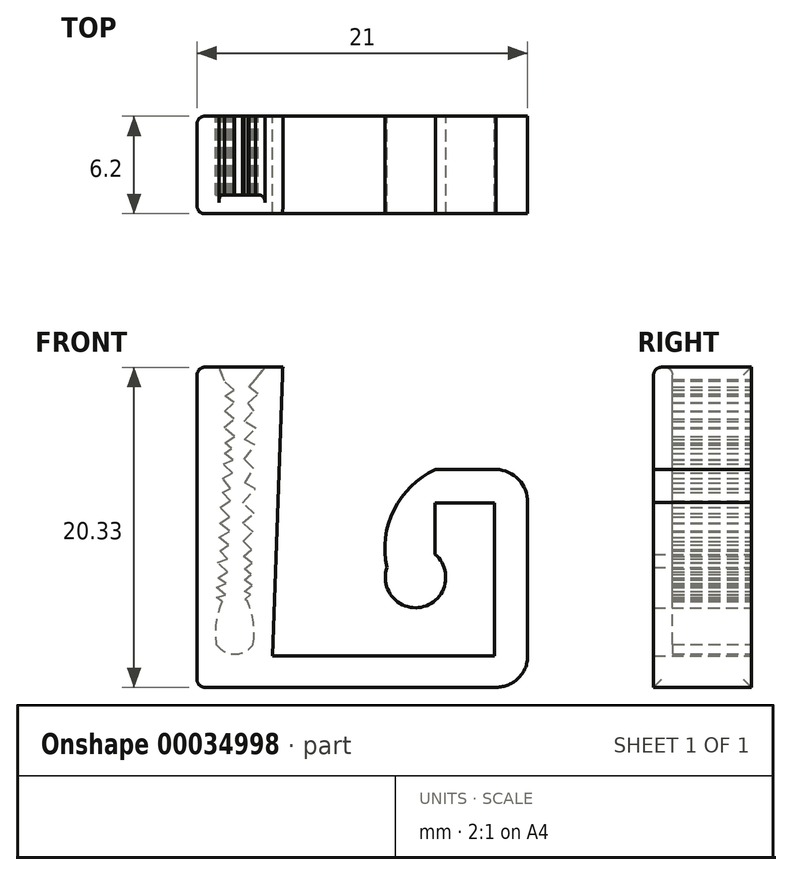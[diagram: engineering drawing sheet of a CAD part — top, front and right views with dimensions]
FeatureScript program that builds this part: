
annotation { "Feature Type Name" : "Feature", "Feature Type Description" : "" }
export const myFeature = defineFeature(function(context is Context, id is Id, definition is map)
    precondition{}
    {
        {
            var Q0;
            Q0=qCreatedBy(makeId("Front.planeOp"),FACE);
            var sketch = newSketch(context, id + "F0", { "sketchPlane" : qUnion([Q0])});
            skLineSegment(sketch, "E0", {"start": v(-28.92, -7.05) * mm, "end": v(-14.82, -7.05) * mm});
            skLineSegment(sketch, "E1", {"start": v(-14.82, -7.05) * mm, "end": v(-14.82, 2.65) * mm});
            skArc(sketch, "E2", {"start": v(-18.58, 4.78) * mm, "mid": v(-21.22, 2.2) * mm, "end": v(-21.65, -1.46) * mm});
            skArc(sketch, "E3", {"start": v(-21.65, -1.46) * mm, "mid": v(-19.32, -3.93) * mm, "end": v(-18.62, -0.6) * mm});
            skLineSegment(sketch, "E4", {"start": v(-18.62, 2.65) * mm, "end": v(-18.62, -0.6) * mm});
            skLineSegment(sketch, "E5.top", {"start": v(-28.92, 11.27) * mm, "end": v(-29.4, 11.27) * mm});
            skLineSegment(sketch, "E6", {"start": v(-18.62, 2.65) * mm, "end": v(-14.82, 2.65) * mm});
            skLineSegment(sketch, "E7", {"start": v(-33.72, 11.27) * mm, "end": v(-33.72, -9.05) * mm});
            skLineSegment(sketch, "E8", {"start": v(-30.52, -7.05) * mm, "end": v(-32.12, -7.05) * mm, "construction": true});
            skLineSegment(sketch, "E9", {"start": v(-21.65, -1.46) * mm, "end": v(-18.62, -0.6) * mm, "construction": true});
            skLineSegment(sketch, "E10", {"start": v(-31.32, -5.22) * mm, "end": v(-31.32, -1.98) * mm, "construction": true});
            skLineSegment(sketch, "E11.MirrorCS", {"start": v(-30.52, 11.27) * mm, "end": v(-32.12, 11.27) * mm, "construction": true});
            skArc(sketch, "E12", {"start": v(-32.12, -3.61) * mm, "mid": v(-32.5, -4.94) * mm, "end": v(-32.5, -6.32) * mm});
            skArc(sketch, "E13", {"start": v(-32.5, -6.32) * mm, "mid": v(-31.32, -6.95) * mm, "end": v(-30.15, -6.32) * mm});
            skArc(sketch, "E14.MirrorCS", {"start": v(-30.52, -3.61) * mm, "mid": v(-30.14, -4.94) * mm, "end": v(-30.15, -6.32) * mm});
            skArc(sketch, "E15", {"start": v(-12.72, 2.65) * mm, "mid": v(-13.28, 4.13) * mm, "end": v(-14.72, 4.78) * mm});
            skLineSegment(sketch, "E16", {"start": v(-14.72, 4.78) * mm, "end": v(-18.58, 4.78) * mm});
            skArc(sketch, "E17", {"start": v(-14.82, -9.05) * mm, "mid": v(-13.34, -8.5) * mm, "end": v(-12.72, -7.05) * mm});
            skLineSegment(sketch, "E18", {"start": v(-14.82, -9.05) * mm, "end": v(-33.72, -9.05) * mm});
            skLineSegment(sketch, "E19", {"start": v(-12.72, -7.05) * mm, "end": v(-12.72, 2.68) * mm});
            skLineSegment(sketch, "E20", {"start": v(-28.92, -7.05) * mm, "end": v(-28.27, 11.27) * mm});
            skLineSegment(sketch, "E21", {"start": v(-28.27, 11.27) * mm, "end": v(-28.92, 11.27) * mm});
            skLineSegment(sketch, "E22", {"start": v(-32.12, -3.61) * mm, "end": v(-32.5, -3.36) * mm});
            skLineSegment(sketch, "E23", {"start": v(-32.5, -3.36) * mm, "end": v(-31.9, -3.2) * mm});
            skLineSegment(sketch, "E24", {"start": v(-31.9, -3.2) * mm, "end": v(-32.47, -2.73) * mm});
            skLineSegment(sketch, "E25", {"start": v(-32.47, -2.73) * mm, "end": v(-31.87, -2.47) * mm});
            skLineSegment(sketch, "E26", {"start": v(-31.87, -2.47) * mm, "end": v(-32.37, -2.11) * mm});
            skLineSegment(sketch, "E27", {"start": v(-32.37, -2.11) * mm, "end": v(-31.8, -1.73) * mm});
            skLineSegment(sketch, "E28", {"start": v(-31.8, -1.73) * mm, "end": v(-32.4, -1.14) * mm});
            skLineSegment(sketch, "E29", {"start": v(-32.4, -1.14) * mm, "end": v(-31.79, -0.91) * mm});
            skLineSegment(sketch, "E30", {"start": v(-31.79, -0.91) * mm, "end": v(-32.26, -0.4) * mm});
            skLineSegment(sketch, "E31", {"start": v(-32.26, -0.4) * mm, "end": v(-31.73, 0) * mm});
            skLineSegment(sketch, "E32", {"start": v(-31.73, 0) * mm, "end": v(-32.3, 0.46) * mm});
            skLineSegment(sketch, "E33", {"start": v(-32.3, 0.46) * mm, "end": v(-31.65, 0.87) * mm});
            skLineSegment(sketch, "E34", {"start": v(-31.65, 0.87) * mm, "end": v(-32.28, 1.36) * mm});
            skLineSegment(sketch, "E35", {"start": v(-32.28, 1.36) * mm, "end": v(-31.67, 1.76) * mm});
            skLineSegment(sketch, "E36", {"start": v(-31.67, 1.76) * mm, "end": v(-32.25, 2.38) * mm});
            skLineSegment(sketch, "E37", {"start": v(-32.25, 2.38) * mm, "end": v(-31.6, 2.77) * mm});
            skLineSegment(sketch, "E38", {"start": v(-31.6, 2.77) * mm, "end": v(-32.08, 3.3) * mm});
            skLineSegment(sketch, "E39", {"start": v(-32.08, 3.3) * mm, "end": v(-31.58, 3.56) * mm});
            skLineSegment(sketch, "E40", {"start": v(-31.58, 3.56) * mm, "end": v(-32.1, 4.22) * mm});
            skLineSegment(sketch, "E41", {"start": v(-32.1, 4.22) * mm, "end": v(-31.45, 4.55) * mm});
            skLineSegment(sketch, "E42", {"start": v(-31.45, 4.55) * mm, "end": v(-32.05, 5.14) * mm});
            skLineSegment(sketch, "E43", {"start": v(-32.05, 5.14) * mm, "end": v(-31.42, 5.37) * mm});
            skLineSegment(sketch, "E44", {"start": v(-31.42, 5.37) * mm, "end": v(-31.96, 5.8) * mm});
            skLineSegment(sketch, "E45", {"start": v(-31.96, 5.8) * mm, "end": v(-31.54, 6.12) * mm});
            skLineSegment(sketch, "E46", {"start": v(-31.54, 6.12) * mm, "end": v(-31.94, 6.47) * mm});
            skLineSegment(sketch, "E47", {"start": v(-31.94, 6.47) * mm, "end": v(-31.32, 6.88) * mm});
            skLineSegment(sketch, "E48", {"start": v(-31.32, 6.88) * mm, "end": v(-32.01, 7.44) * mm});
            skLineSegment(sketch, "E49", {"start": v(-32.01, 7.44) * mm, "end": v(-31.35, 7.98) * mm});
            skLineSegment(sketch, "E50", {"start": v(-31.35, 7.98) * mm, "end": v(-31.96, 8.46) * mm});
            skLineSegment(sketch, "E51", {"start": v(-31.96, 8.46) * mm, "end": v(-31.38, 9.02) * mm});
            skLineSegment(sketch, "E52", {"start": v(-31.38, 9.02) * mm, "end": v(-31.93, 9.43) * mm});
            skLineSegment(sketch, "E53", {"start": v(-31.93, 9.43) * mm, "end": v(-31.38, 9.83) * mm});
            skLineSegment(sketch, "E54", {"start": v(-31.38, 9.83) * mm, "end": v(-31.97, 10.39) * mm});
            skLineSegment(sketch, "E55", {"start": v(-30.52, -3.61) * mm, "end": v(-30.66, -3.49) * mm});
            skLineSegment(sketch, "E56", {"start": v(-30.66, -3.49) * mm, "end": v(-30.3, -3.14) * mm});
            skLineSegment(sketch, "E57", {"start": v(-30.3, -3.14) * mm, "end": v(-30.69, -2.97) * mm});
            skLineSegment(sketch, "E58", {"start": v(-30.69, -2.97) * mm, "end": v(-30.24, -2.58) * mm});
            skLineSegment(sketch, "E59", {"start": v(-30.24, -2.58) * mm, "end": v(-30.7, -2.24) * mm});
            skLineSegment(sketch, "E60", {"start": v(-30.7, -2.24) * mm, "end": v(-30.27, -1.87) * mm});
            skLineSegment(sketch, "E61", {"start": v(-30.27, -1.87) * mm, "end": v(-30.7, -1.53) * mm});
            skLineSegment(sketch, "E62", {"start": v(-30.7, -1.53) * mm, "end": v(-30.22, -1.16) * mm});
            skLineSegment(sketch, "E63", {"start": v(-30.22, -1.16) * mm, "end": v(-30.76, -0.74) * mm});
            skLineSegment(sketch, "E64", {"start": v(-30.76, -0.74) * mm, "end": v(-30.24, -0.31) * mm});
            skLineSegment(sketch, "E65", {"start": v(-30.24, -0.31) * mm, "end": v(-30.79, 0.22) * mm});
            skLineSegment(sketch, "E66", {"start": v(-30.79, 0.22) * mm, "end": v(-30.15, 0.82) * mm});
            skLineSegment(sketch, "E67", {"start": v(-30.15, 0.82) * mm, "end": v(-30.83, 1.4) * mm});
            skLineSegment(sketch, "E68", {"start": v(-30.83, 1.4) * mm, "end": v(-30.1, 2) * mm});
            skLineSegment(sketch, "E69", {"start": v(-30.1, 2) * mm, "end": v(-30.84, 2.67) * mm});
            skLineSegment(sketch, "E70", {"start": v(-30.84, 2.67) * mm, "end": v(-30.01, 3.55) * mm});
            skLineSegment(sketch, "E71", {"start": v(-30.01, 3.55) * mm, "end": v(-30.68, 3.92) * mm});
            skLineSegment(sketch, "E72", {"start": v(-30.68, 3.92) * mm, "end": v(-30.13, 4.84) * mm});
            skLineSegment(sketch, "E73", {"start": v(-30.13, 4.84) * mm, "end": v(-30.72, 5.42) * mm});
            skLineSegment(sketch, "E74", {"start": v(-30.72, 5.42) * mm, "end": v(-30.04, 6.32) * mm});
            skLineSegment(sketch, "E75", {"start": v(-30.04, 6.32) * mm, "end": v(-30.7, 6.7) * mm});
            skLineSegment(sketch, "E76", {"start": v(-30.7, 6.7) * mm, "end": v(-29.98, 7.38) * mm});
            skLineSegment(sketch, "E77", {"start": v(-29.98, 7.38) * mm, "end": v(-30.73, 7.84) * mm});
            skLineSegment(sketch, "E78", {"start": v(-30.73, 7.84) * mm, "end": v(-30.11, 8.5) * mm});
            skLineSegment(sketch, "E79", {"start": v(-30.11, 8.5) * mm, "end": v(-30.46, 9) * mm});
            skLineSegment(sketch, "E80", {"start": v(-30.46, 9) * mm, "end": v(-29.84, 9.59) * mm});
            skLineSegment(sketch, "E81", {"start": v(-29.84, 9.59) * mm, "end": v(-30.41, 10.01) * mm});
            skLineSegment(sketch, "E82", {"start": v(-30.41, 10.01) * mm, "end": v(-30, 10.48) * mm});
            skLineSegment(sketch, "E83", {"start": v(-30, 10.48) * mm, "end": v(-29.4, 11.27) * mm});
            skLineSegment(sketch, "E84", {"start": v(-31.97, 10.39) * mm, "end": v(-32.33, 11.27) * mm});
            skLineSegment(sketch, "E85", {"start": v(-32.33, 11.27) * mm, "end": v(-33.72, 11.27) * mm});
            skSolve(sketch);
        }
        {
            var Q0;
            Q0 = qSketchRegion(id + "F0", true);
            extrude(context, id + "F1", {"entities" : qUnion([Q0]), "depth" : 5 * mm});
        }
        {
            var Q0;
            Q0=makeQuery(id+"F1.opExtrude","CAP_FACE",FACE,{"disambiguationData":[OSD([sQuery(id+"F0.wireOp",EDGE,"E0"),sQuery(id+"F0.wireOp",EDGE,"E1"),sQuery(id+"F0.wireOp",EDGE,"E2"),sQuery(id+"F0.wireOp",EDGE,"E3"),sQuery(id+"F0.wireOp",EDGE,"E4"),sQuery(id+"F0.wireOp",EDGE,"E5.top"),sQuery(id+"F0.wireOp",EDGE,"E6"),sQuery(id+"F0.wireOp",EDGE,"b5f2b3c7-c1ca-4791-923c-05a685cb43df"),sQuery(id+"F0.wireOp",EDGE,"E7"),sQuery(id+"F0.wireOp",EDGE,"aed927df-a92d-4f69-8dc8-6bdfb17ffc2d"),sQuery(id+"F0.wireOp",EDGE,"E12"),sQuery(id+"F0.wireOp",EDGE,"E13"),sQuery(id+"F0.wireOp",EDGE,"E14.MirrorCS"),sQuery(id+"F0.wireOp",EDGE,"b6acafe8-4966-4914-a1c4-64246340acb0"),sQuery(id+"F0.wireOp",EDGE,"36ad4d8f-950c-4962-8cc0-d44bfbabf640"),sQuery(id+"F0.wireOp",EDGE,"E15"),sQuery(id+"F0.wireOp",EDGE,"E16"),sQuery(id+"F0.wireOp",EDGE,"E17"),sQuery(id+"F0.wireOp",EDGE,"E18"),sQuery(id+"F0.wireOp",EDGE,"E19"),sQuery(id+"F0.wireOp",EDGE,"E20"),sQuery(id+"F0.wireOp",EDGE,"E21")])],"isStart":false});
            var sketch = newSketch(context, id + "F2", { "sketchPlane" : qUnion([Q0])});
            skLineSegment(sketch, "E86.bottom", {"start": v(-32.7, -7.05) * mm, "end": v(-29.4, -7.05) * mm});
            skLineSegment(sketch, "E86.top", {"start": v(-32.7, 11.27) * mm, "end": v(-29.4, 11.27) * mm});
            skLineSegment(sketch, "E86.left", {"start": v(-32.7, -7.05) * mm, "end": v(-32.7, 11.27) * mm});
            skLineSegment(sketch, "E86.right", {"start": v(-29.4, -7.05) * mm, "end": v(-29.4, 11.27) * mm});
            skSolve(sketch);
        }
        {
            var Q0;
            Q0=makeQuery(id+"F2.imprint","IMPRINT",FACE,{"disambiguationData":[TD([[makeQuery(id+"F2.imprint","IMPRINT",EDGE,{"derivedFrom":sQuery(id+"F2.wireOp",EDGE,"E86.bottom")}),1.0]])]});
            var Q1;
            {var subQ3=makeQuery(id+"F1.opExtrude","CAP_EDGE",EDGE,{"disambiguationData":[OSD([sQuery(id+"F0.wireOp",EDGE,"E12")])],"isStart":false});Q1=makeQuery(id+"F2.imprint","IMPRINT",FACE,{"disambiguationData":[TD([[makeQuery(id+"F2.imprint","IMPRINT",EDGE,{"derivedFrom":subQ3}),1.0]])]});}
            var Q2;
            {var subQ3=makeQuery(id+"F1.opExtrude","CAP_EDGE",EDGE,{"disambiguationData":[OSD([sQuery(id+"F0.wireOp",EDGE,"b6acafe8-4966-4914-a1c4-64246340acb0")])],"isStart":false});Q2=makeQuery(id+"F2.imprint","IMPRINT",FACE,{"disambiguationData":[TD([[makeQuery(id+"F2.imprint","IMPRINT",EDGE,{"derivedFrom":subQ3}),1.0]])]});}
            var Q3;
            Q3=makeQuery(id+"F2.imprint","IMPRINT",FACE,{"disambiguationData":[TD([[makeQuery(id+"F2.imprint","IMPRINT",EDGE,{"derivedFrom":sQuery(id+"F2.wireOp",EDGE,"E86.bottom")}),-1.0]])]});
            var Q4;
            {var subQ6=makeQuery(id+"F1.opExtrude","CAP_EDGE",EDGE,{"disambiguationData":[OSD([sQuery(id+"F0.wireOp",EDGE,"E82")])],"isStart":false});Q4=makeQuery(id+"F2.imprint","IMPRINT",FACE,{"disambiguationData":[TD([[makeQuery(id+"F2.imprint","IMPRINT",EDGE,{"derivedFrom":subQ6}),-1.0]])]});}
            extrude(context, id + "F3", {"entities" : qUnion([Q0, Q1, Q2, Q3, Q4]), "operationType" : NewBodyOperationType.ADD, "depth" : 1.2 * mm});
        }
        {
            var Q0;
            Q0=makeQuery(id+"F3.opExtrude","CAP_EDGE",EDGE,{"disambiguationData":[OSD([sQuery(id+"F0.wireOp",EDGE,"E5.top"),sQuery(id+"F0.wireOp",EDGE,"b5f2b3c7-c1ca-4791-923c-05a685cb43df"),sQuery(id+"F0.wireOp",EDGE,"aed927df-a92d-4f69-8dc8-6bdfb17ffc2d"),sQuery(id+"F0.wireOp",EDGE,"E21"),sQuery(id+"F2.wireOp",EDGE,"E86.top")])],"isStart":true});
            fillet(context, id + "F4", {"entities" : qUnion([Q0]), "radius" : 0.5 * mm, "tangentPropagation" : true, "allowEdgeOverflow" : false});
        }
        {
            var Q0;
            {var subQ0=sQuery(id+"F0.wireOp",EDGE,"b5f2b3c7-c1ca-4791-923c-05a685cb43df");var subQ1=sQuery(id+"F0.wireOp",EDGE,"E7");Q0=makeQuery(id+"F3.boolean.opBoolean","MERGE",EDGE,{"derivedFrom":[makeQuery(id+"F1.opExtrude","SWEPT_EDGE",EDGE,{"disambiguationData":[OSD([subQ0,subQ1])]}),makeQuery(id+"F3.opExtrude","SWEPT_EDGE",EDGE,{"disambiguationData":[OSD([subQ0,subQ1,sQuery(id+"F0.wireOp",EDGE,"aed927df-a92d-4f69-8dc8-6bdfb17ffc2d")])]})]});}
            var Q1;
            Q1=makeQuery(id+"F1.opExtrude","CAP_EDGE",EDGE,{"disambiguationData":[OSD([sQuery(id+"F0.wireOp",EDGE,"E7")])],"isStart":true});
            var Q2;
            Q2=makeQuery(id+"F3.opExtrude","CAP_EDGE",EDGE,{"disambiguationData":[OSD([sQuery(id+"F0.wireOp",EDGE,"E7")])],"isStart":false});
            var Q3;
            {var subQ0=sQuery(id+"F0.wireOp",EDGE,"E7");var subQ1=sQuery(id+"F0.wireOp",EDGE,"E18");Q3=makeQuery(id+"F3.boolean.opBoolean","MERGE",EDGE,{"derivedFrom":[makeQuery(id+"F1.opExtrude","SWEPT_EDGE",EDGE,{"disambiguationData":[OSD([subQ0,subQ1])]}),makeQuery(id+"F3.opExtrude","SWEPT_EDGE",EDGE,{"disambiguationData":[OSD([subQ0,subQ1])]})]});}
            var Q4;
            Q4=makeQuery(id+"F3.opExtrude","CAP_EDGE",EDGE,{"disambiguationData":[OSD([sQuery(id+"F0.wireOp",EDGE,"E5.top"),sQuery(id+"F0.wireOp",EDGE,"b5f2b3c7-c1ca-4791-923c-05a685cb43df"),sQuery(id+"F0.wireOp",EDGE,"aed927df-a92d-4f69-8dc8-6bdfb17ffc2d"),sQuery(id+"F0.wireOp",EDGE,"E21"),sQuery(id+"F2.wireOp",EDGE,"E86.top")])],"isStart":false});
            fillet(context, id + "F5", {"entities" : qUnion([Q0, Q1, Q2, Q3, Q4]), "radius" : 0.5 * mm, "tangentPropagation" : true, "allowEdgeOverflow" : false});
        }
    });
